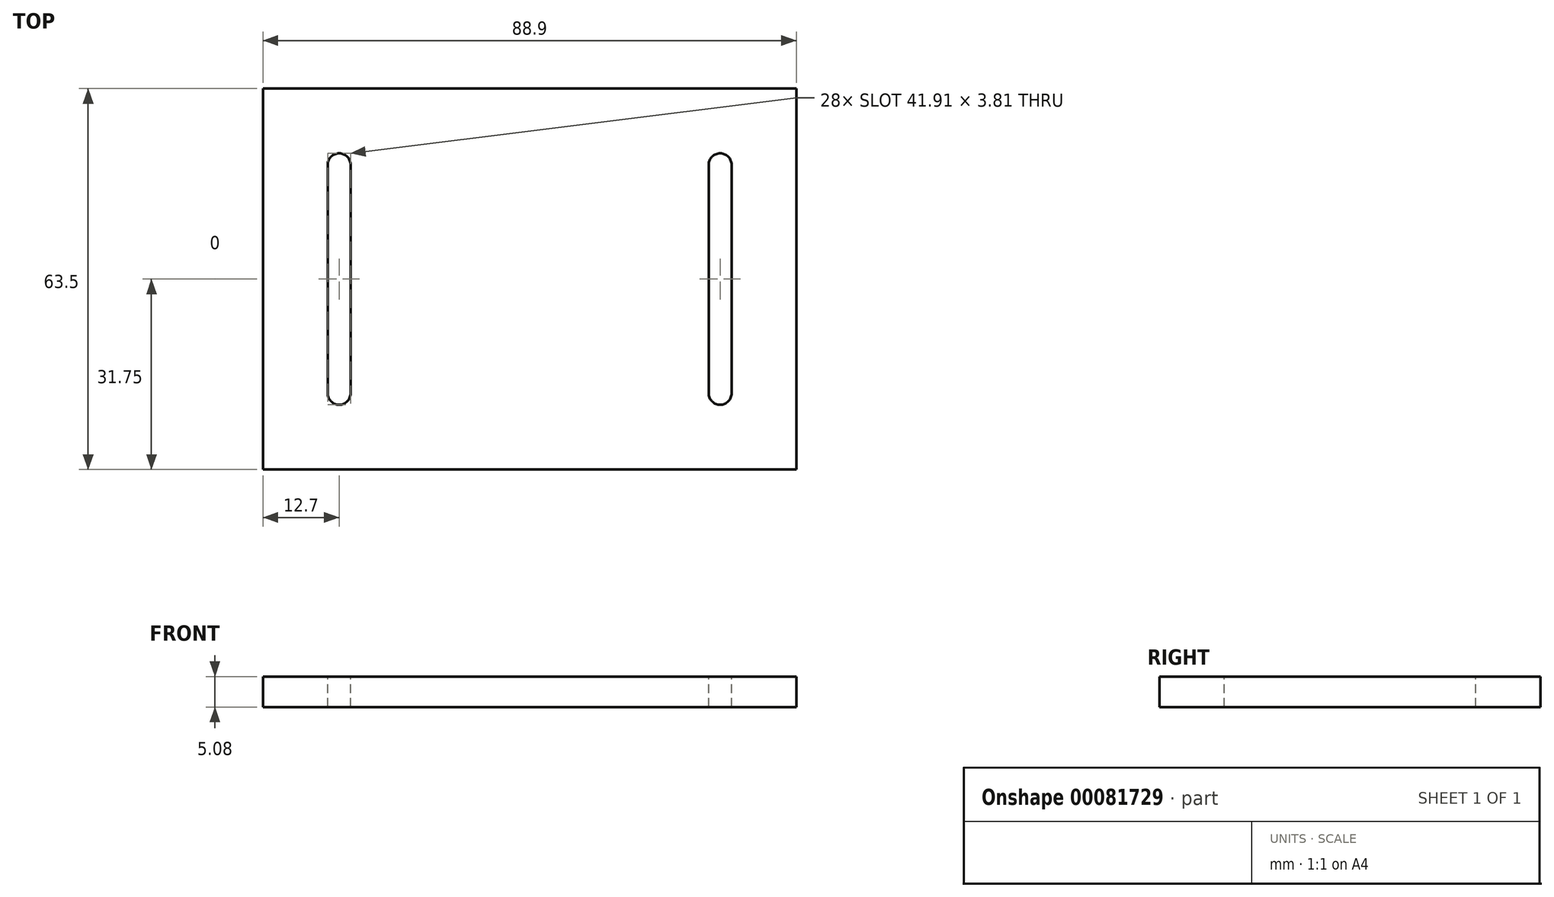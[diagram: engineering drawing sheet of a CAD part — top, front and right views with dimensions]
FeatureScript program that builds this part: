
annotation { "Feature Type Name" : "Feature", "Feature Type Description" : "" }
export const myFeature = defineFeature(function(context is Context, id is Id, definition is map)
    precondition{}
    {
        {
            var Q0;
            Q0=qCreatedBy(makeId("Top.planeOp"),FACE);
            var sketch = newSketch(context, id + "F0", { "sketchPlane" : qUnion([Q0])});
            skLineSegment(sketch, "E0.bottom", {"start": v(0, 0) * mm, "end": v(88.9, 0) * mm});
            skLineSegment(sketch, "E0.top", {"start": v(0, 63.5) * mm, "end": v(88.9, 63.5) * mm});
            skLineSegment(sketch, "E0.left", {"start": v(0, 0) * mm, "end": v(0, 63.5) * mm});
            skLineSegment(sketch, "E0.right", {"start": v(88.9, 0) * mm, "end": v(88.9, 63.5) * mm});
            skSolve(sketch);
        }
        {
            var Q0;
            Q0 = qSketchRegion(id + "F0", true);
            extrude(context, id + "F1", {"entities" : qUnion([Q0]), "depth" : 5.08 * mm});
        }
        {
            var Q0;
            Q0=makeQuery(id+"F1.opExtrude","CAP_FACE",FACE,{"disambiguationData":[OSD([sQuery(id+"F0.wireOp",EDGE,"E0.bottom"),sQuery(id+"F0.wireOp",EDGE,"E0.top"),sQuery(id+"F0.wireOp",EDGE,"E0.left"),sQuery(id+"F0.wireOp",EDGE,"E0.right")])],"isStart":false});
            var sketch = newSketch(context, id + "F2", { "sketchPlane" : qUnion([Q0])});
            skLineSegment(sketch, "E1.left", {"start": v(10.8, 50.8) * mm, "end": v(10.8, 12.7) * mm});
            skLineSegment(sketch, "E1.right", {"start": v(14.6, 50.8) * mm, "end": v(14.6, 12.7) * mm});
            skLineSegment(sketch, "E2.left", {"start": v(74.3, 50.8) * mm, "end": v(74.3, 12.7) * mm});
            skLineSegment(sketch, "E2.right", {"start": v(78.1, 50.8) * mm, "end": v(78.1, 12.7) * mm});
            skArc(sketch, "E3", {"start": v(10.8, 12.7) * mm, "mid": v(12.7, 10.8) * mm, "end": v(14.6, 12.7) * mm});
            skArc(sketch, "E4", {"start": v(74.3, 12.7) * mm, "mid": v(76.2, 10.8) * mm, "end": v(78.1, 12.7) * mm});
            skArc(sketch, "E5", {"start": v(14.6, 50.8) * mm, "mid": v(12.7, 52.7) * mm, "end": v(10.8, 50.8) * mm});
            skArc(sketch, "E6", {"start": v(78.1, 50.8) * mm, "mid": v(76.2, 52.7) * mm, "end": v(74.3, 50.8) * mm});
            skSolve(sketch);
        }
        {
            var Q0;
            Q0 = qSketchRegion(id + "F2", true);
            extrude(context, id + "F3", {"entities" : qUnion([Q0]), "operationType" : NewBodyOperationType.REMOVE, "endBound" : BoundingType.THROUGH_ALL, "oppositeDirection" : true, "depth" : 25.4 * mm});
        }
    });
